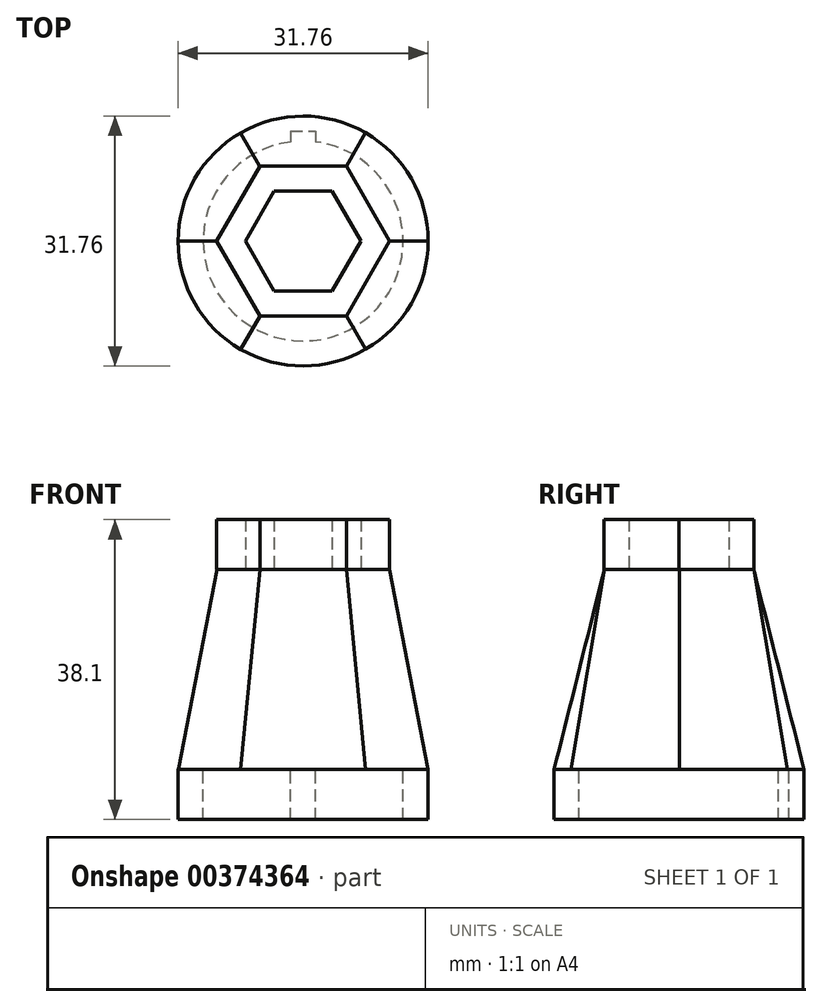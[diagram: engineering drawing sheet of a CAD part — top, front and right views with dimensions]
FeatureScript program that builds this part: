
annotation { "Feature Type Name" : "Feature", "Feature Type Description" : "" }
export const myFeature = defineFeature(function(context is Context, id is Id, definition is map)
    precondition{}
    {
        {
            var Q0;
            Q0=qCreatedBy(makeId("Top.planeOp"),FACE);
            cPlane(context, id + "F0", {"entities" : qUnion([Q0]), "cplaneType" : CPlaneType.OFFSET, "offset" : 25.4 * mm, "width" : 152.4 * mm, "height" : 152.4 * mm});
        }
        {
            var Q0;
            Q0=qCreatedBy(id+"F0.planeOp",FACE);
            var sketch = newSketch(context, id + "F1", { "sketchPlane" : qUnion([Q0])});
            skCircle(sketch, "E0.cCircle", {"center": v(0, 0) * mm, "radius": 9.53 * mm, "construction": true});
            skLineSegment(sketch, "E0.0", {"start": v(5.5, 9.52) * mm, "end": v(11, 0) * mm});
            skLineSegment(sketch, "E0.1", {"start": v(11, 0) * mm, "end": v(5.5, -9.53) * mm});
            skLineSegment(sketch, "E0.2", {"start": v(5.5, -9.53) * mm, "end": v(-5.5, -9.53) * mm});
            skLineSegment(sketch, "E0.3", {"start": v(-5.5, -9.53) * mm, "end": v(-11, 0) * mm});
            skLineSegment(sketch, "E0.4", {"start": v(-11, 0) * mm, "end": v(-5.5, 9.53) * mm});
            skLineSegment(sketch, "E0.5", {"start": v(-5.5, 9.53) * mm, "end": v(5.5, 9.53) * mm});
            skPoint(sketch, "E0.0.midPoint", {"position": v(8.25, 4.76) * mm});
            skLineSegment(sketch, "E1.0", {"start": v(-7.33, 0) * mm, "end": v(-3.67, 6.35) * mm});
            skLineSegment(sketch, "E1.1", {"start": v(3.67, 6.35) * mm, "end": v(7.33, 0) * mm});
            skLineSegment(sketch, "E1.2", {"start": v(7.33, 0) * mm, "end": v(3.67, -6.35) * mm});
            skLineSegment(sketch, "E1.3", {"start": v(-3.67, 6.35) * mm, "end": v(3.67, 6.35) * mm});
            skLineSegment(sketch, "E1.4", {"start": v(3.67, -6.35) * mm, "end": v(-3.67, -6.35) * mm});
            skLineSegment(sketch, "E1.5", {"start": v(-3.67, -6.35) * mm, "end": v(-7.33, 0) * mm});
            skSolve(sketch);
        }
        {
            var Q0;
            Q0=qCreatedBy(makeId("Top.planeOp"),FACE);
            var sketch = newSketch(context, id + "F2", { "sketchPlane" : qUnion([Q0])});
            skCircle(sketch, "E2", {"center": v(0, 0) * mm, "radius": 15.88 * mm});
            skSolve(sketch);
        }
        {
            var Q0;
            Q0=qCreatedBy(id+"F0.planeOp",FACE);
            var sketch = newSketch(context, id + "F3", { "sketchPlane" : qUnion([Q0])});
            skCircle(sketch, "E3.cCircle", {"center": v(0, 0) * mm, "radius": 9.5 * mm, "construction": true});
            skLineSegment(sketch, "E3.0", {"start": v(10.96, 0.01) * mm, "end": v(5.5, -9.49) * mm});
            skLineSegment(sketch, "E3.1", {"start": v(5.5, -9.49) * mm, "end": v(-5.47, -9.5) * mm});
            skLineSegment(sketch, "E3.2", {"start": v(-5.47, -9.5) * mm, "end": v(-10.96, -0.01) * mm});
            skLineSegment(sketch, "E3.3", {"start": v(-10.96, -0.01) * mm, "end": v(-5.5, 9.49) * mm});
            skLineSegment(sketch, "E3.4", {"start": v(-5.5, 9.49) * mm, "end": v(5.47, 9.5) * mm});
            skLineSegment(sketch, "E3.5", {"start": v(5.47, 9.5) * mm, "end": v(10.96, 0.01) * mm});
            skPoint(sketch, "E3.0.midPoint", {"position": v(8.23, -4.74) * mm});
            skSolve(sketch);
        }
        {
            var Q0;
            Q0 = qSketchRegion(id + "F2", true);
            var Q1;
            Q1 = qSketchRegion(id + "F3", true);
            loft(context, id + "F4", {"sheetProfilesArray" : [{ "sheetProfileEntities" : qUnion([Q0]) }, { "sheetProfileEntities" : qUnion([Q1]) }]});
        }
        {
            var Q0;
            Q0 = qSketchRegion(id + "F1", true);
            extrude(context, id + "F5", {"entities" : qUnion([Q0]), "operationType" : NewBodyOperationType.ADD, "depth" : 6.35 * mm});
        }
        {
            var Q0;
            Q0=qCreatedBy(makeId("Top.planeOp"),FACE);
            var sketch = newSketch(context, id + "F6", { "sketchPlane" : qUnion([Q0])});
            skCircle(sketch, "E4", {"center": v(0, 0) * mm, "radius": 15.88 * mm});
            skCircle(sketch, "E5", {"center": v(0, 0) * mm, "radius": 12.7 * mm});
            skLineSegment(sketch, "E6.bottom", {"start": v(-1.59, 13.97) * mm, "end": v(1.59, 13.97) * mm});
            skLineSegment(sketch, "E6.left", {"start": v(-1.59, 13.97) * mm, "end": v(-1.59, 12.6) * mm});
            skLineSegment(sketch, "E6.right", {"start": v(1.59, 13.97) * mm, "end": v(1.59, 12.6) * mm});
            skPoint(sketch, "E6.middle", {"position": v(0, 12.7) * mm});
            skLineSegment(sketch, "E7", {"start": v(0, 0) * mm, "end": v(0, 15.88) * mm, "construction": true});
            skPoint(sketch, "E8", {"position": v(0, 13.97) * mm});
            skSolve(sketch);
        }
        {
            var Q0;
            Q0 = qSketchRegion(id + "F6", true);
            extrude(context, id + "F7", {"entities" : qUnion([Q0]), "operationType" : NewBodyOperationType.ADD, "oppositeDirection" : true, "depth" : 6.35 * mm});
        }
    });
